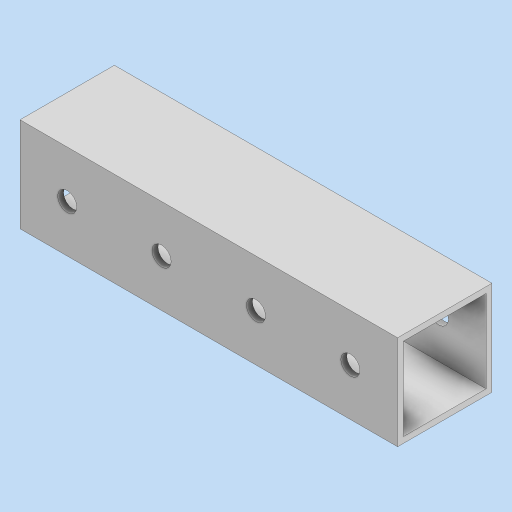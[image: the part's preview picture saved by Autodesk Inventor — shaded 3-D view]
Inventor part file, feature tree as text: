
AUTODESK INVENTOR PART (.ipt)
format: ipt  version: 2024 (Build 280153000, 153)  size: 123,904 bytes
history: native  units: in
note: dims shown in document units (in); Inventor stores cm internally (conversion verified against a paired STEP export)
features: extrude x2, sketch x2, projected_geometry x1
ambient origin geometry x8: Origin, YZ Plane, XZ Plane, XY Plane, X Axis, Y Axis, Z Axis, Center Point
bodies: Solid1 (feature_tree)
feature tree (5):
  extrude  "Extrusion1"  Depth=1.0in
  extrude  "Extrusion3"  Depth=4.0in TaperAngle=0.0deg
  sketch  "Sketch1"  dims[d0=1.0in d1=1.0in]
  sketch  "Sketch3"  dims[d2=0.0625in d3=4.0in d4=0.0in d14=0.203in d15=0.203in d16=0.5in d17=1.0in d18=1.0in d19=0.0in d20=0.5in d21=1.0in d22=1.0in]
  projected_geometry  "Projected Loop1"
